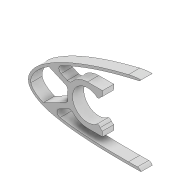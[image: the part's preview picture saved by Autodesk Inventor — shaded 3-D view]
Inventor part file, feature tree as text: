
AUTODESK INVENTOR PART (.ipt)
format: ipt  version: 2022 (Build 260153000, 153)  size: 465,408 bytes
history: native  units: mm
features: extrude x10, sketch x9, projected_geometry x6, shell x2, fillet x2
ambient origin geometry x8: Origin, YZ Plane, XZ Plane, XY Plane, X Axis, Y Axis, Z Axis, Center Point
bodies: Solid1 (feature_tree)
feature tree (29):
  extrude  "Extrusion1"  Depth=5.0mm
  shell  "Shell1"  Thickness=6.0mm
  extrude  "Extrusion2"  Depth=2.0mm
  extrude  "Extrusion3"  Depth=5.9mm
  extrude  "Extrusion4"  Depth=10.0mm TaperAngle=0.0deg
  extrude  "Extrusion5"  Depth=10.0mm TaperAngle=0.0deg
  extrude  "Extrusion7"  Depth=5.0mm
  sketch  "Sketch16"  dims[d20=5.0mm d21=5.0mm]
  extrude  "Extrusion8"  Depth=5.0mm
  extrude  "Extrusion9"  Depth=2.0mm
  shell  "Shell2"  Thickness=2.0mm
  extrude  "Extrusion11"  Depth=45.0mm
  fillet  "Fillet1"  Radius=10.0mm
  extrude  "Extrusion12"  Depth=4.5mm TaperAngle=0.0deg
  fillet  "Fillet2"  Radius=1.0mm
  sketch  "Sketch3"  dims[d0=4.5mm d1=0.0mm d2=5.0mm d3=6.0mm]
  sketch  "Sketch7"  dims[d5=4.5mm d6=0.0mm d7=2.0mm]
  projected_geometry  "Projected Loop3"
  sketch  "Sketch8"  dims[d8=2.0mm d9=5.9mm]
  sketch  "Sketch9"  dims[d12=4.0mm d13=10.0mm d14=0.0mm]
  sketch  "Sketch10"  dims[d15=40.0mm d16=10.0mm d17=0.0mm]
  projected_geometry  "Projected Loop4"
  sketch  "Sketch14"  dims[d18=5.0mm d19=5.0mm]
  projected_geometry  "Projected Loop7"
  projected_geometry  "Projected Loop9"
  sketch  "Sketch25"  dims[d22=4.5mm d23=0.0mm d24=2.0mm d26=2.0mm]
  projected_geometry  "Projected Loop12"
  sketch  "Sketch26"  dims[d29=4.5mm d30=0.0mm d31=45.0mm d32=10.0mm d33=0.0mm d34=4.5mm d35=0.0mm d36=1.0mm d43=12.0mm d45=3.756mm d46=23.606mm d47=2.0mm d48=2.0mm d49=2.0mm d50=6.0mm d51=6.0mm d52=1.5mm d53=1.5mm d54=1.0mm d55=1.0mm d56=4.5mm d57=0.0mm d58=1.5mm d59=4.5mm d60=0.0mm d61=1.5mm]
  projected_geometry  "Projected Loop13"
